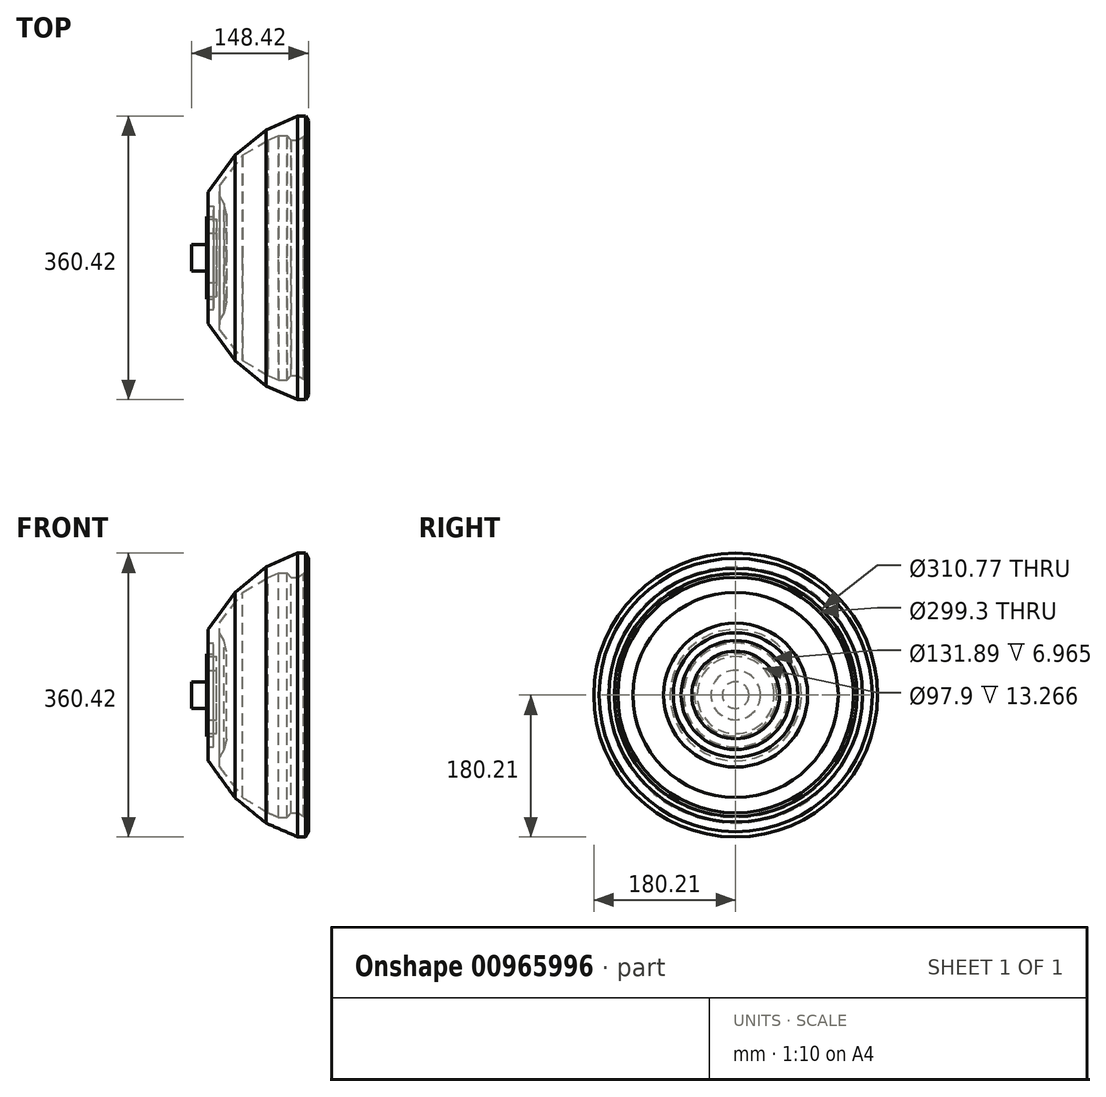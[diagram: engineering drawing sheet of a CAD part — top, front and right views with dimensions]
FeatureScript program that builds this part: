
annotation { "Feature Type Name" : "Feature", "Feature Type Description" : "" }
export const myFeature = defineFeature(function(context is Context, id is Id, definition is map)
    precondition{}
    {
        {
            var Q0;
            Q0=qCreatedBy(makeId("Front.planeOp"),FACE);
            var sketch = newSketch(context, id + "F0", { "sketchPlane" : qUnion([Q0])});
            skLineSegment(sketch, "E0", {"start": v(0, 0) * mm, "end": v(0, 16.91) * mm});
            skLineSegment(sketch, "E1", {"start": v(0, 16.91) * mm, "end": v(18.74, 16.91) * mm});
            skLineSegment(sketch, "E2", {"start": v(18.74, 16.91) * mm, "end": v(18.74, 31.43) * mm});
            skLineSegment(sketch, "E3", {"start": v(18.74, 31.43) * mm, "end": v(32, 31.43) * mm});
            skLineSegment(sketch, "E4", {"start": v(32, 31.43) * mm, "end": v(32, 48.95) * mm});
            skLineSegment(sketch, "E5", {"start": v(32, 48.95) * mm, "end": v(18.74, 48.95) * mm});
            skLineSegment(sketch, "E6", {"start": v(18.74, 48.95) * mm, "end": v(18.74, 52.31) * mm});
            skLineSegment(sketch, "E7", {"start": v(18.74, 52.31) * mm, "end": v(28.03, 52.31) * mm});
            skLineSegment(sketch, "E8", {"start": v(28.03, 52.31) * mm, "end": v(28.03, 65.95) * mm});
            skLineSegment(sketch, "E9", {"start": v(28.03, 65.95) * mm, "end": v(21.06, 65.95) * mm});
            skLineSegment(sketch, "E10", {"start": v(21.06, 65.95) * mm, "end": v(21.06, 83.45) * mm});
            skLineSegment(sketch, "E11", {"start": v(21.06, 83.45) * mm, "end": v(54.89, 130.27) * mm});
            skLineSegment(sketch, "E12", {"start": v(54.89, 130.27) * mm, "end": v(94.36, 162.56) * mm});
            skLineSegment(sketch, "E13", {"start": v(94.36, 162.56) * mm, "end": v(134.82, 180.2) * mm});
            skLineSegment(sketch, "E14", {"start": v(134.82, 180.2) * mm, "end": v(144.77, 180.2) * mm});
            skLineSegment(sketch, "E15", {"start": v(144.77, 180.2) * mm, "end": v(148.42, 173.52) * mm});
            skLineSegment(sketch, "E16", {"start": v(148.42, 173.52) * mm, "end": v(148.42, 161.1) * mm});
            skLineSegment(sketch, "E17", {"start": v(148.42, 161.1) * mm, "end": v(142.45, 154.22) * mm});
            skLineSegment(sketch, "E18", {"start": v(142.45, 154.22) * mm, "end": v(134.82, 149.65) * mm});
            skLineSegment(sketch, "E19", {"start": v(134.82, 149.65) * mm, "end": v(126.2, 149.65) * mm});
            skLineSegment(sketch, "E20", {"start": v(126.2, 149.65) * mm, "end": v(121.22, 155.39) * mm});
            skLineSegment(sketch, "E21", {"start": v(121.22, 155.39) * mm, "end": v(110.6, 155.39) * mm});
            skLineSegment(sketch, "E22", {"start": v(110.6, 155.39) * mm, "end": v(97.34, 149.65) * mm});
            skLineSegment(sketch, "E23", {"start": v(97.34, 149.65) * mm, "end": v(64.84, 130.27) * mm});
            skLineSegment(sketch, "E24", {"start": v(64.84, 130.27) * mm, "end": v(35.32, 91.45) * mm});
            skLineSegment(sketch, "E25", {"start": v(35.32, 91.45) * mm, "end": v(35.32, 79.18) * mm});
            skLineSegment(sketch, "E26", {"start": v(35.32, 79.18) * mm, "end": v(40.96, 69.2) * mm});
            skLineSegment(sketch, "E27", {"start": v(40.96, 69.2) * mm, "end": v(44.6, 55.66) * mm});
            skLineSegment(sketch, "E28", {"start": v(44.6, 55.66) * mm, "end": v(44.6, 38.32) * mm});
            skLineSegment(sketch, "E29", {"start": v(44.6, 38.32) * mm, "end": v(44.6, 21.26) * mm});
            skLineSegment(sketch, "E30", {"start": v(44.6, 21.26) * mm, "end": v(44.6, 0) * mm});
            skLineSegment(sketch, "E31", {"start": v(44.6, 0) * mm, "end": v(0, 0) * mm});
            skSolve(sketch);
        }
        {
            var Q0;
            Q0 = qSketchRegion(id + "F0", true);
            var Q1;
            Q1=sQuery(id+"F0.wireOp",EDGE,"E31");
            revolve(context, id + "F1", {"surfaceOperationType" : NewSurfaceOperationType.NEW, "entities" : qUnion([Q0]), "axis" : qUnion([Q1]), "revolveType" : RevolveType.FULL});
        }
    });
